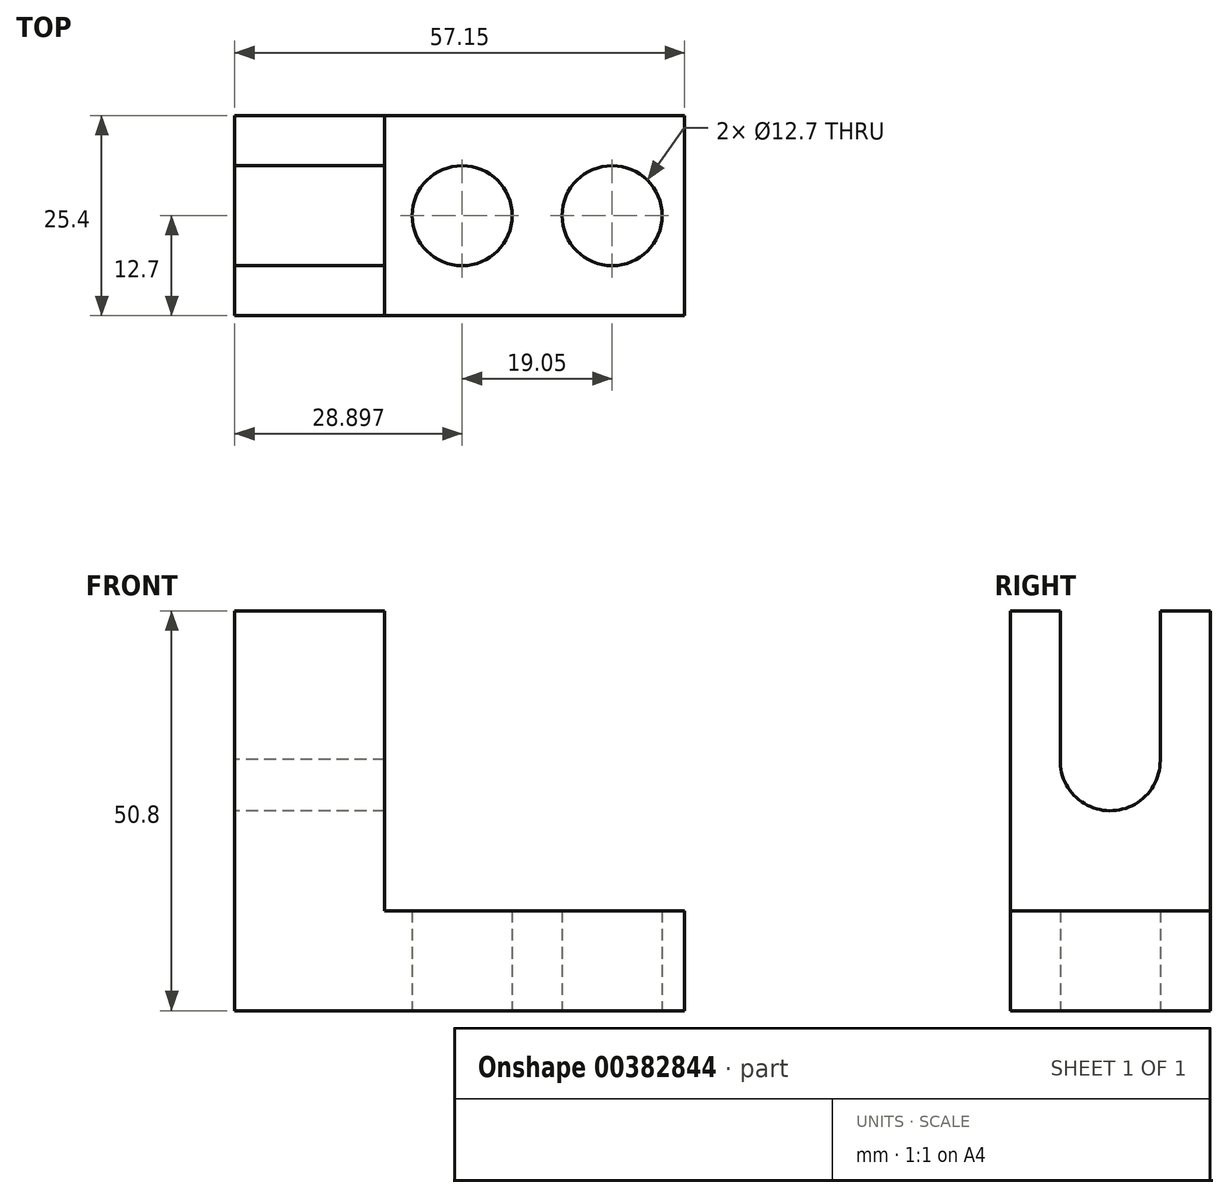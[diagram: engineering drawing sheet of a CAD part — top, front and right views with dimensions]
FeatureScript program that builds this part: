
annotation { "Feature Type Name" : "Feature", "Feature Type Description" : "" }
export const myFeature = defineFeature(function(context is Context, id is Id, definition is map)
    precondition{}
    {
        {
            var Q0;
            Q0=qCreatedBy(makeId("Front.planeOp"),FACE);
            var sketch = newSketch(context, id + "F0", { "sketchPlane" : qUnion([Q0])});
            skLineSegment(sketch, "E0", {"start": v(0, 0) * mm, "end": v(57.15, 0) * mm});
            skLineSegment(sketch, "E1", {"start": v(57.15, 0) * mm, "end": v(57.15, 12.7) * mm});
            skLineSegment(sketch, "E2", {"start": v(57.15, 12.7) * mm, "end": v(19.05, 12.7) * mm});
            skLineSegment(sketch, "E3", {"start": v(19.05, 12.7) * mm, "end": v(19.05, 50.8) * mm});
            skLineSegment(sketch, "E4", {"start": v(19.05, 50.8) * mm, "end": v(0, 50.8) * mm});
            skLineSegment(sketch, "E5", {"start": v(0, 50.8) * mm, "end": v(0, 0) * mm});
            skSolve(sketch);
        }
        {
            var Q0;
            Q0 = qSketchRegion(id + "F0", true);
            extrude(context, id + "F1", {"entities" : qUnion([Q0]), "depth" : 25.4 * mm});
        }
        {
            var Q0;
            Q0=qCreatedBy(makeId("Top.planeOp"),FACE);
            var sketch = newSketch(context, id + "F2", { "sketchPlane" : qUnion([Q0])});
            skCircle(sketch, "E6", {"center": v(28.9, -12.7) * mm, "radius": 6.35 * mm});
            skCircle(sketch, "E7", {"center": v(47.95, -12.7) * mm, "radius": 6.35 * mm});
            skSolve(sketch);
        }
        {
            var Q0;
            Q0 = qSketchRegion(id + "F2", true);
            extrude(context, id + "F3", {"entities" : qUnion([Q0]), "operationType" : NewBodyOperationType.REMOVE, "depth" : 25.4 * mm});
        }
        {
            var Q0;
            Q0=qCreatedBy(makeId("Right.planeOp"),FACE);
            var sketch = newSketch(context, id + "F4", { "sketchPlane" : qUnion([Q0])});
            skCircle(sketch, "E8", {"center": v(-12.7, 31.75) * mm, "radius": 6.35 * mm});
            skLineSegment(sketch, "E9", {"start": v(-19.05, 31.92) * mm, "end": v(-19.05, 50.8) * mm});
            skLineSegment(sketch, "E10", {"start": v(-6.35, 31.72) * mm, "end": v(-6.35, 50.8) * mm});
            skLineSegment(sketch, "E11", {"start": v(-19.05, 50.8) * mm, "end": v(-6.35, 50.8) * mm});
            skSolve(sketch);
        }
        {
            var Q0;
            Q0 = qSketchRegion(id + "F4", true);
            extrude(context, id + "F5", {"entities" : qUnion([Q0]), "operationType" : NewBodyOperationType.REMOVE, "depth" : 25.4 * mm});
        }
    });
